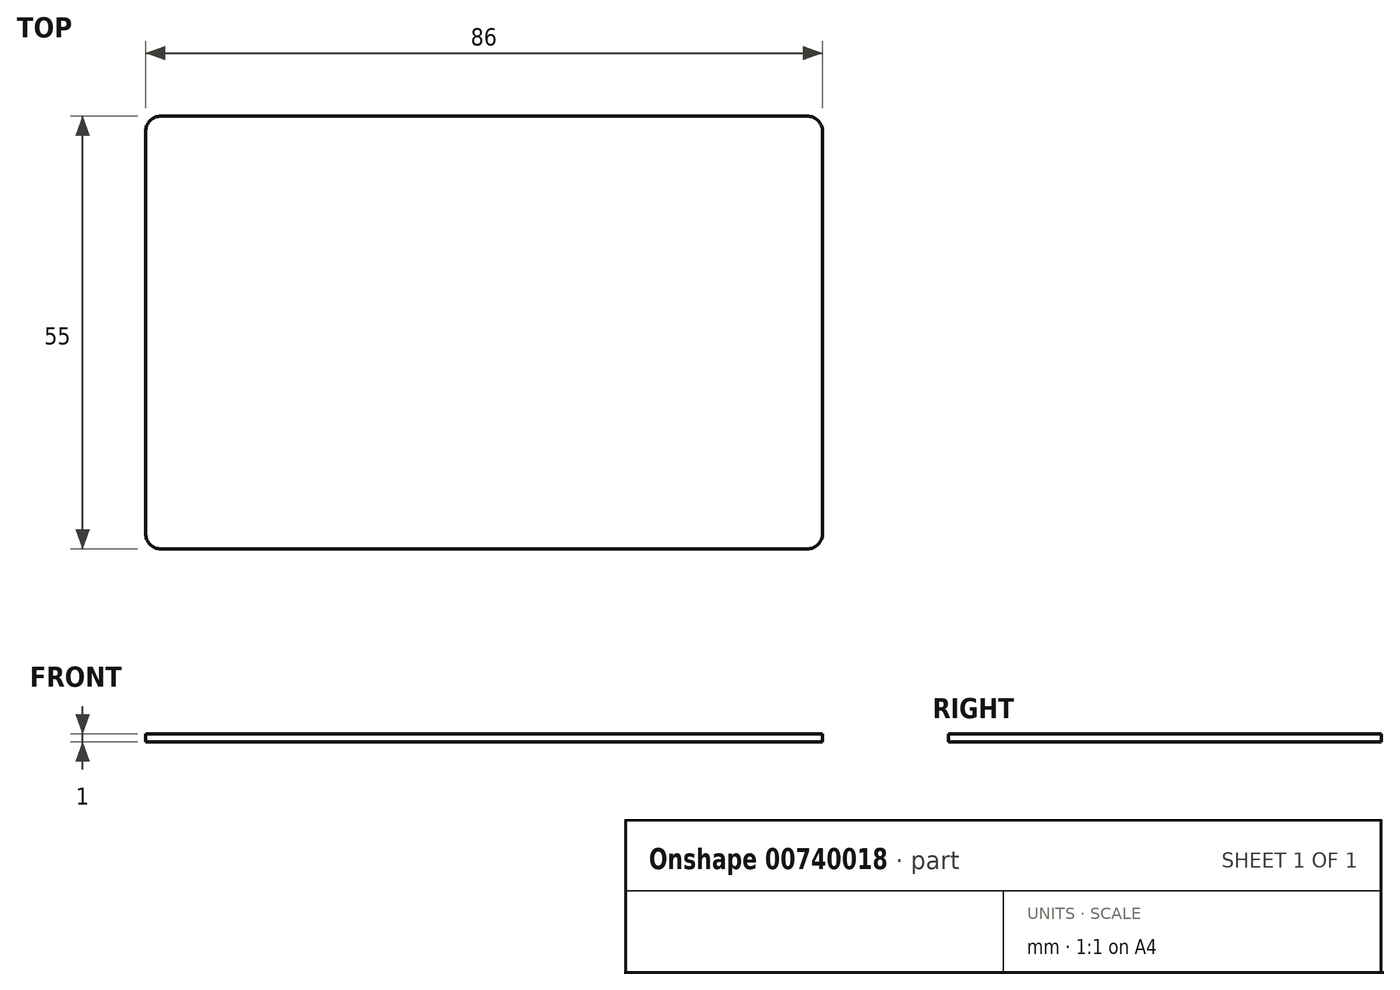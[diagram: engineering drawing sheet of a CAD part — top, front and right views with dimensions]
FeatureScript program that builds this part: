
annotation { "Feature Type Name" : "Feature", "Feature Type Description" : "" }
export const myFeature = defineFeature(function(context is Context, id is Id, definition is map)
    precondition{}
    {
        {
            var Q0;
            Q0=qCreatedBy(makeId("Top.planeOp"),FACE);
            var sketch = newSketch(context, id + "F0", { "sketchPlane" : qUnion([Q0])});
            skLineSegment(sketch, "E0.bottom", {"start": v(-171.3, 120.4) * mm, "end": v(-89.3, 120.4) * mm});
            skLineSegment(sketch, "E0.top", {"start": v(-171.3, 65.4) * mm, "end": v(-89.3, 65.4) * mm});
            skLineSegment(sketch, "E0.left", {"start": v(-173.3, 118.4) * mm, "end": v(-173.3, 67.4) * mm});
            skLineSegment(sketch, "E0.right", {"start": v(-87.3, 118.4) * mm, "end": v(-87.3, 67.4) * mm});
            skPoint(sketch, "E1.visualSharp", {"position": v(-173.3, 120.4) * mm});
            skArc(sketch, "E1.filletArc", {"start": v(-171.3, 120.4) * mm, "mid": v(-172.7, 119.82) * mm, "end": v(-173.3, 118.4) * mm});
            skPoint(sketch, "E2.visualSharp", {"position": v(-87.3, 120.4) * mm});
            skArc(sketch, "E2.filletArc", {"start": v(-87.3, 118.4) * mm, "mid": v(-87.88, 119.82) * mm, "end": v(-89.3, 120.4) * mm});
            skPoint(sketch, "E3.visualSharp", {"position": v(-87.3, 65.4) * mm});
            skArc(sketch, "E3.filletArc", {"start": v(-89.3, 65.4) * mm, "mid": v(-87.88, 66) * mm, "end": v(-87.3, 67.4) * mm});
            skPoint(sketch, "E4.visualSharp", {"position": v(-173.3, 65.4) * mm});
            skArc(sketch, "E4.filletArc", {"start": v(-173.3, 67.4) * mm, "mid": v(-172.7, 66) * mm, "end": v(-171.3, 65.4) * mm});
            skSolve(sketch);
        }
        {
            var Q0;
            Q0 = qSketchRegion(id + "F0", true);
            extrude(context, id + "F1", {"entities" : qUnion([Q0]), "depth" : 1 * mm, "offsetDistance" : 25 * mm});
        }
    });
